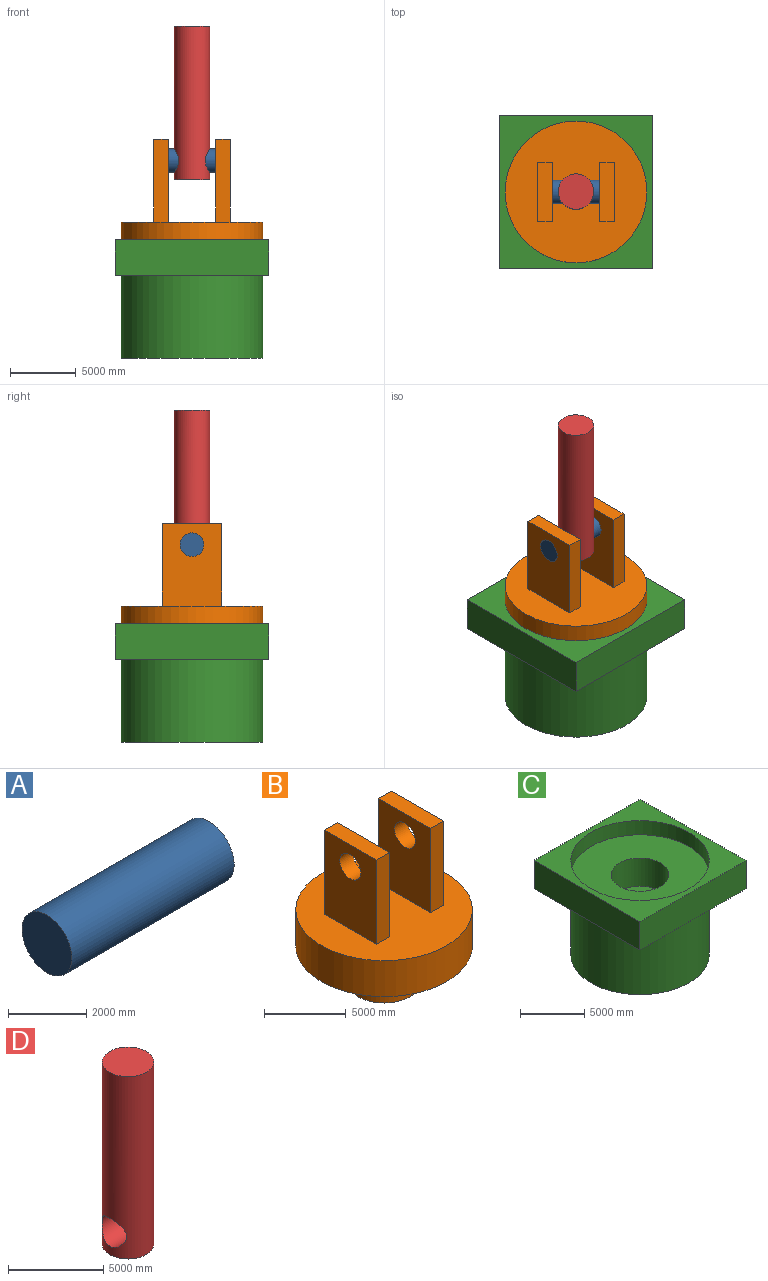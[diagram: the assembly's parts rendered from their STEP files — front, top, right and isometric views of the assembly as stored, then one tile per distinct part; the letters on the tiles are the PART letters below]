
ASSEMBLY  parts=4 mates=3
PART A: 3 faces, bbox 5850x1800x1800 mm
  f0: plane 1800x1800mm, normal (-1,0,0), area 2544690mm2, adj f1
  f1: cylinder r=900mm len=5850mm, axis (1,0,0), area 33080970.6mm2, adj f0,f2
  f2: plane 1800x1800mm, normal (1,0,0), area 2544690mm2, adj f1
PART B: 17 faces, bbox 10800x10800x11700 mm
  f0: plane 10800x10800mm, normal (0,0,1), area 81483841.8mm2, adj f1,f3,f4,f5,f6,f8,f9,f10
  f1: cylinder r=5400mm len=10800mm, axis (0,0,-1), area 91608841.8mm2, adj f0,f2
  f2: plane 10800x10800mm, normal (0,0,-1), area 75704529mm2, adj f1,f13
  f3: plane 6300x4500mm, normal (-1,0,0), area 25805310mm2, adj f0,f4,f6,f7,f16
  f4: plane 6300x1125mm, normal (0,-1,0), area 7087500mm2, adj f0,f3,f5,f7
  f5: plane 6300x4500mm, normal (1,0,0), area 25805310mm2, adj f0,f4,f6,f7,f16
  f6: plane 6300x1125mm, normal (0,1,0), area 7087500mm2, adj f0,f3,f5,f7
  f7: plane 4500x1125mm, normal (0,0,1), area 5062500mm2, adj f3,f4,f5,f6
  f8: plane 6300x1125mm, normal (0,1,0), area 7087500mm2, adj f0,f9,f11,f12
  f9: plane 6300x4500mm, normal (-1,0,0), area 25805310mm2, adj f0,f8,f10,f12,f15
  f10: plane 6300x1125mm, normal (0,-1,0), area 7087500mm2, adj f0,f9,f11,f12
  f11: plane 6300x4500mm, normal (1,0,0), area 25805310mm2, adj f0,f8,f10,f12,f15
  f12: plane 4500x1125mm, normal (0,0,1), area 5062500mm2, adj f8,f9,f10,f11
  f13: cylinder r=2250mm len=4500mm, axis (0,0,1), area 38170350.7mm2, adj f2,f14
  f14: plane 4500x4500mm, normal (0,0,-1), area 15904312.8mm2, adj f13
  f15: cylinder r=900mm len=1800mm, axis (1,0,0), area 6361725.1mm2, adj f9,f11
  f16: cylinder r=900mm len=1800mm, axis (1,0,0), area 6361725.1mm2, adj f3,f5
PART C: 12 faces, bbox 11700x11700x9000 mm
  f0: plane 11700x2700mm, normal (1,0,0), area 31590000mm2, adj f1,f3,f4,f5
  f1: plane 11700x2700mm, normal (0,1,0), area 31590000mm2, adj f0,f2,f4,f5
  f2: plane 11700x2700mm, normal (-1,0,0), area 31590000mm2, adj f1,f3,f4,f5
  f3: plane 11700x2700mm, normal (0,-1,0), area 31590000mm2, adj f0,f2,f4,f5
  f4: plane 11700x11700mm, normal (0,0,1), area 45281158.2mm2, adj f0,f1,f2,f3,f8
  f5: plane 11700x11700mm, normal (0,0,-1), area 45281158.2mm2, adj f0,f1,f2,f3,f6
  f6: cylinder r=5400mm len=10800mm, axis (0,0,1), area 213753964.2mm2, adj f5,f7
  f7: plane 10800x10800mm, normal (0,0,-1), area 91608841.8mm2, adj f6
  f8: cylinder r=5400mm len=10800mm, axis (0,0,-1), area 45804420.9mm2, adj f4,f9
  f9: plane 10800x10800mm, normal (0,0,1), area 75704529mm2, adj f8,f10
  f10: cylinder r=2250mm len=4500mm, axis (0,0,1), area 38170350.7mm2, adj f9,f11
  f11: plane 4500x4500mm, normal (0,0,1), area 15904312.8mm2, adj f10
PART D: 4 faces, bbox 2700x2700x11700 mm
  f0: cylinder r=1350mm len=11700mm, axis (0,0,-1), area 93812789.2mm2, adj f1,f2,f3
  f1: plane 2700x2700mm, normal (0,0,1), area 5725552.6mm2, adj f0
  f2: plane 2700x2700mm, normal (0,0,-1), area 5725552.6mm2, adj f0
  f3: cylinder r=900mm len=2700.01mm, axis (1,0,0), area 13393440.8mm2, adj f0
PLACE A rot(axis=(0.08,0.99,0.14),0deg) t=(0,0,0)mm
PLACE B at identity
PLACE C at identity fixed
PLACE D rot(axis=(0.08,0.99,0.14),0deg) t=(-0.07,0,0)mm
MATE revolute B.f1 <-> C.f6  axis (0,0,-1) through (0,0,-1350)mm
MATE revolute A.f1 <-> B.f15  axis (1,0,0) through (2925,0,8730)mm
MATE fastened D.f3 <-> A.f1  axis (1,0,0) through (0,0,8730)mm
